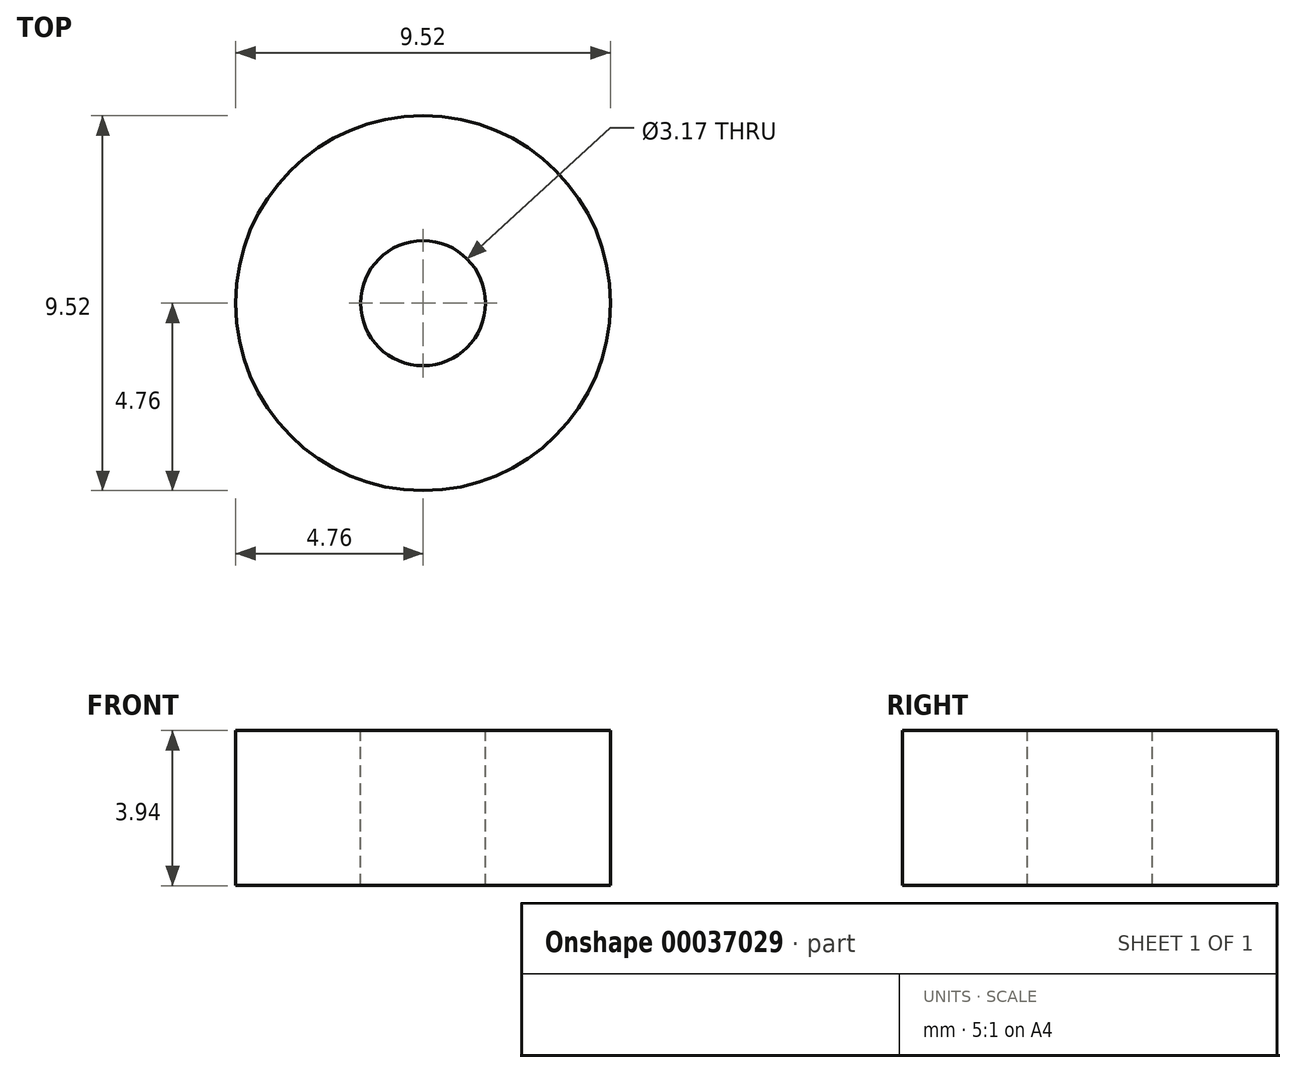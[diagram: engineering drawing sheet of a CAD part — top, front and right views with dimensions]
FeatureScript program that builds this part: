
annotation { "Feature Type Name" : "Feature", "Feature Type Description" : "" }
export const myFeature = defineFeature(function(context is Context, id is Id, definition is map)
    precondition{}
    {
        {
            var Q0;
            Q0=qCreatedBy(makeId("Front.planeOp"),FACE);
            var sketch = newSketch(context, id + "F0", { "sketchPlane" : qUnion([Q0])});
            skLineSegment(sketch, "E0", {"start": v(0, 1.97) * mm, "end": v(0, -1.97) * mm, "construction": true});
            skLineSegment(sketch, "E1", {"start": v(0, 1.97) * mm, "end": v(1.59, 1.97) * mm, "construction": true});
            skLineSegment(sketch, "E2", {"start": v(0, -1.97) * mm, "end": v(1.59, -1.97) * mm, "construction": true});
            skLineSegment(sketch, "E3", {"start": v(1.59, -1.97) * mm, "end": v(1.59, 1.97) * mm});
            skLineSegment(sketch, "E4", {"start": v(1.59, 1.97) * mm, "end": v(4.76, 1.97) * mm});
            skLineSegment(sketch, "E5", {"start": v(4.76, 1.97) * mm, "end": v(4.76, -1.97) * mm});
            skLineSegment(sketch, "E6", {"start": v(4.76, -1.97) * mm, "end": v(1.59, -1.97) * mm});
            skSolve(sketch);
        }
        {
            var Q0;
            Q0 = qSketchRegion(id + "F0", true);
            var Q1;
            Q1=sQuery(id+"F0.wireOp",EDGE,"E0");
            revolve(context, id + "F1", {"entities" : qUnion([Q0]), "axis" : qUnion([Q1]), "revolveType" : RevolveType.FULL});
        }
    });
